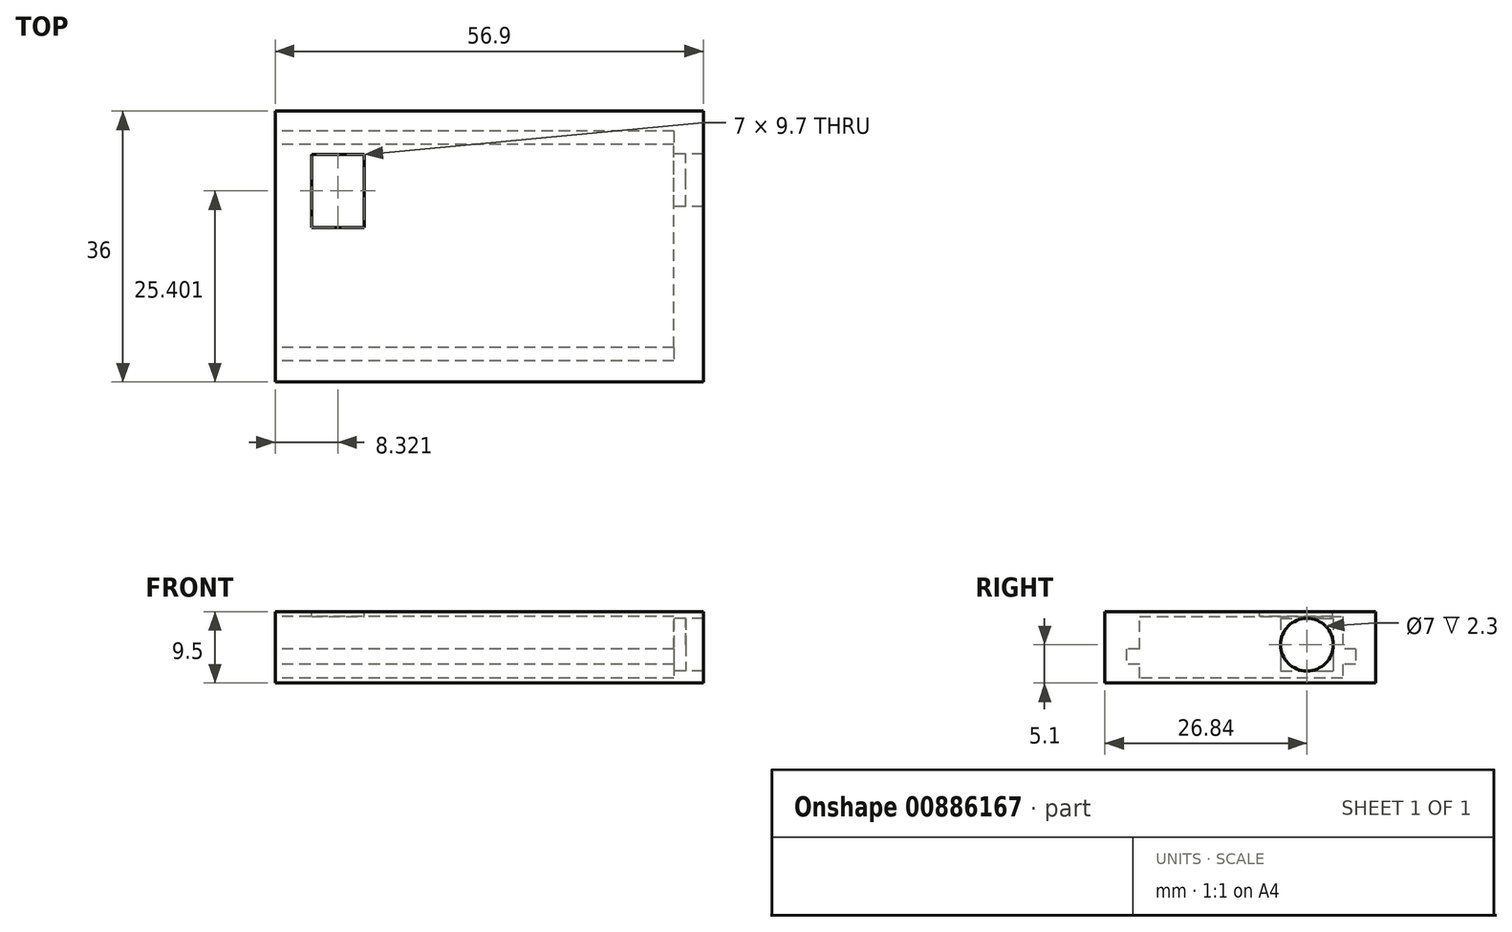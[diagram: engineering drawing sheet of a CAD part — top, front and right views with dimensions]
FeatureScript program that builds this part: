
annotation { "Feature Type Name" : "Feature", "Feature Type Description" : "" }
export const myFeature = defineFeature(function(context is Context, id is Id, definition is map)
    precondition{}
    {
        {
            var Q0;
            Q0=qCreatedBy(makeId("Top.planeOp"),FACE);
            var sketch = newSketch(context, id + "F0", { "sketchPlane" : qUnion([Q0])});
            skLineSegment(sketch, "E0.bottom", {"start": v(-26.94, 14.91) * mm, "end": v(23.06, 14.91) * mm});
            skLineSegment(sketch, "E0.top", {"start": v(-26.94, -15.09) * mm, "end": v(23.06, -15.09) * mm});
            skLineSegment(sketch, "E0.left", {"start": v(-26.94, 14.91) * mm, "end": v(-26.94, -15.09) * mm});
            skLineSegment(sketch, "E0.right", {"start": v(23.06, 14.91) * mm, "end": v(23.06, -15.09) * mm});
            skLineSegment(sketch, "E1.bottom", {"start": v(-34, -4.69) * mm, "end": v(-26.94, -4.69) * mm});
            skLineSegment(sketch, "E1.top", {"start": v(-34, -11.69) * mm, "end": v(-26.94, -11.69) * mm});
            skLineSegment(sketch, "E1.left", {"start": v(-34, -4.69) * mm, "end": v(-34, -11.69) * mm});
            skLineSegment(sketch, "E1.right", {"start": v(-26.94, -4.69) * mm, "end": v(-26.94, -11.69) * mm});
            skLineSegment(sketch, "E2.0", {"start": v(-26.94, 17.91) * mm, "end": v(26.06, 17.91) * mm});
            skLineSegment(sketch, "E2.2", {"start": v(-26.94, -18.09) * mm, "end": v(26.06, -18.09) * mm});
            skLineSegment(sketch, "E2.3", {"start": v(26.06, 17.91) * mm, "end": v(26.06, -18.09) * mm});
            skLineSegment(sketch, "E3", {"start": v(-26.94, 17.91) * mm, "end": v(-26.94, 14.91) * mm});
            skLineSegment(sketch, "E4", {"start": v(-26.94, -18.09) * mm, "end": v(-26.94, -15.09) * mm});
            skSolve(sketch);
        }
        {
            var Q0;
            {var subQ3=sQuery(id+"F0.wireOp",EDGE,"E0.bottom");Q0=makeQuery(id+"F0.imprint","IMPRINT",FACE,{"disambiguationData":[TD([[makeQuery(id+"F0.imprint","IMPRINT",EDGE,{"derivedFrom":subQ3}),-1.0]])]});}
            var Q1;
            {var subQ10=sQuery(id+"F0.wireOp",EDGE,"E0.bottom");Q1=makeQuery(id+"F0.imprint","IMPRINT",FACE,{"disambiguationData":[TD([[makeQuery(id+"F0.imprint","IMPRINT",EDGE,{"derivedFrom":subQ10}),1.0]])]});}
            extrude(context, id + "F1", {"entities" : qUnion([Q0, Q1]), "depth" : 6 * mm, "offsetDistance" : 25 * mm, "hasSecondDirection" : true, "secondDirectionOppositeDirection" : true, "secondDirectionDepth" : 3.5 * mm});
        }
        {
            var Q0;
            Q0=makeQuery(id+"F1.opExtrude","SWEPT_FACE",FACE,{"disambiguationData":[OSD([sQuery(id+"F0.wireOp",EDGE,"E0.left"),sQuery(id+"F0.wireOp",EDGE,"E1.right"),sQuery(id+"F0.wireOp",EDGE,"E3"),sQuery(id+"F0.wireOp",EDGE,"E4")])]});
            var sketch = newSketch(context, id + "F2", { "sketchPlane" : qUnion([Q0])});
            skLineSegment(sketch, "E5", {"start": v(-13.5, 5.34) * mm, "end": v(13.5, 5.34) * mm});
            skLineSegment(sketch, "E6", {"start": v(13.5, 5.34) * mm, "end": v(13.5, -2.86) * mm});
            skLineSegment(sketch, "E7", {"start": v(13.5, -2.86) * mm, "end": v(-13.5, -2.86) * mm});
            skLineSegment(sketch, "E8", {"start": v(-13.5, -2.86) * mm, "end": v(-13.5, 5.34) * mm});
            skPoint(sketch, "E9", {"position": v(0, -2.86) * mm});
            skLineSegment(sketch, "E10.bottom", {"start": v(15.25, -1) * mm, "end": v(-15.25, -1) * mm});
            skLineSegment(sketch, "E10.top", {"start": v(15.25, 1) * mm, "end": v(-15.25, 1) * mm});
            skLineSegment(sketch, "E10.left", {"start": v(15.25, -1) * mm, "end": v(15.25, 1) * mm});
            skLineSegment(sketch, "E10.right", {"start": v(-15.25, -1) * mm, "end": v(-15.25, 1) * mm});
            skPoint(sketch, "E10.middle", {"position": v(0, 0) * mm});
            skSolve(sketch);
        }
        {
            var Q0;
            {var subQ5=sQuery(id+"F2.wireOp",EDGE,"E10.left");Q0=makeQuery(id+"F2.imprint","IMPRINT",FACE,{"disambiguationData":[TD([[makeQuery(id+"F2.imprint","IMPRINT",EDGE,{"derivedFrom":subQ5}),1.0]])]});}
            var Q1;
            {var subQ0=sQuery(id+"F2.wireOp",EDGE,"E7");Q1=makeQuery(id+"F2.imprint","IMPRINT",FACE,{"disambiguationData":[TD([[makeQuery(id+"F2.imprint","IMPRINT",EDGE,{"derivedFrom":subQ0}),-1.0]])]});}
            var Q2;
            {var subQ5=sQuery(id+"F2.wireOp",EDGE,"E10.right");Q2=makeQuery(id+"F2.imprint","IMPRINT",FACE,{"disambiguationData":[TD([[makeQuery(id+"F2.imprint","IMPRINT",EDGE,{"derivedFrom":subQ5}),-1.0]])]});}
            var Q3;
            {var subQ0=sQuery(id+"F2.wireOp",EDGE,"E10.top");var subQ1=sQuery(id+"F2.wireOp",EDGE,"E6");var subQ2=makeQuery(id+"F2.imprint","INTERSECT",VERTEX,{"derivedFrom":[subQ1,subQ0]});Q3=makeQuery(id+"F2.imprint","IMPRINT",FACE,{"disambiguationData":[TD([[makeQuery(id+"F2.imprint","IMPRINT",EDGE,{"disambiguationData":[TD([[subQ2,-1.0]])],"derivedFrom":subQ1}),-1.0]])]});}
            var Q4;
            {var subQ0=sQuery(id+"F2.wireOp",EDGE,"E5");Q4=makeQuery(id+"F2.imprint","IMPRINT",FACE,{"disambiguationData":[TD([[makeQuery(id+"F2.imprint","IMPRINT",EDGE,{"derivedFrom":subQ0}),-1.0]])]});}
            extrude(context, id + "F3", {"entities" : qUnion([Q0, Q1, Q2, Q3, Q4]), "operationType" : NewBodyOperationType.REMOVE, "endBound" : BoundingType.THROUGH_ALL, "oppositeDirection" : true, "depth" : 25 * mm, "offsetDistance" : 25 * mm});
        }
        {
            var Q0;
            Q0=makeQuery(id+"F1.opExtrude","CAP_FACE",FACE,{"disambiguationData":[OSD([sQuery(id+"F0.wireOp",EDGE,"E2.0"),sQuery(id+"F0.wireOp",EDGE,"E2.1"),sQuery(id+"F0.wireOp",EDGE,"E2.2"),sQuery(id+"F0.wireOp",EDGE,"E2.3")])],"isStart":false});
            var sketch = newSketch(context, id + "F4", { "sketchPlane" : qUnion([Q0])});
            skLineSegment(sketch, "E11.bottom", {"start": v(-22.12, 12.16) * mm, "end": v(-15.12, 12.16) * mm});
            skLineSegment(sketch, "E11.top", {"start": v(-22.12, 2.46) * mm, "end": v(-15.12, 2.46) * mm});
            skLineSegment(sketch, "E11.left", {"start": v(-22.12, 12.16) * mm, "end": v(-22.12, 2.46) * mm});
            skLineSegment(sketch, "E11.right", {"start": v(-15.12, 12.16) * mm, "end": v(-15.12, 2.46) * mm});
            skSolve(sketch);
        }
        {
            var Q0;
            Q0=makeQuery(id+"F4.imprint","IMPRINT",FACE,{"disambiguationData":[TD([[makeQuery(id+"F4.imprint","IMPRINT",EDGE,{"derivedFrom":sQuery(id+"F4.wireOp",EDGE,"E11.bottom")}),-1.0]])]});
            extrude(context, id + "F5", {"entities" : qUnion([Q0]), "operationType" : NewBodyOperationType.REMOVE, "endBound" : BoundingType.UP_TO_NEXT, "oppositeDirection" : true, "depth" : 25 * mm, "offsetDistance" : 25 * mm});
        }
        {
            var Q0;
            Q0=makeQuery(id+"F1.opExtrude","SWEPT_FACE",FACE,{"disambiguationData":[OSD([sQuery(id+"F0.wireOp",EDGE,"E2.3")])]});
            var sketch = newSketch(context, id + "F6", { "sketchPlane" : qUnion([Q0])});
            skLineSegment(sketch, "E12.0", {"start": v(17.91, 6) * mm, "end": v(-18.09, 6) * mm});
            skLineSegment(sketch, "E12.1", {"start": v(17.91, 6) * mm, "end": v(17.91, -3.5) * mm});
            skLineSegment(sketch, "E12.2", {"start": v(17.91, -3.5) * mm, "end": v(-18.09, -3.5) * mm});
            skLineSegment(sketch, "E12.3", {"start": v(-18.09, 6) * mm, "end": v(-18.09, -3.5) * mm});
            skLineSegment(sketch, "E13", {"start": v(-18.09, 0) * mm, "end": v(17.91, 0) * mm, "construction": true});
            skPoint(sketch, "E13.endSnap0", {"position": v(-15.25, 0) * mm});
            skPoint(sketch, "E14", {"position": v(15.25, 0) * mm});
            skLineSegment(sketch, "E15.bottom", {"start": v(5.25, 5.1) * mm, "end": v(12.25, 5.1) * mm});
            skLineSegment(sketch, "E15.top", {"start": v(5.25, -1.9) * mm, "end": v(12.25, -1.9) * mm});
            skLineSegment(sketch, "E15.left", {"start": v(5.25, 5.1) * mm, "end": v(5.25, -1.9) * mm});
            skLineSegment(sketch, "E15.right", {"start": v(12.25, 5.1) * mm, "end": v(12.25, -1.9) * mm});
            skCircle(sketch, "E16", {"center": v(8.75, 1.6) * mm, "radius": 3.5 * mm});
            skSolve(sketch);
        }
        {
            var Q0;
            Q0=makeQuery(id+"F6.imprint","IMPRINT",FACE,{"disambiguationData":[TD([[makeQuery(id+"F6.imprint","IMPRINT",EDGE,{"derivedFrom":sQuery(id+"F6.wireOp",EDGE,"E12.0")}),1.0]])]});
            var Q1;
            {var subQ0=sQuery(id+"F6.wireOp",EDGE,"E15.left");var subQ1=sQuery(id+"F6.wireOp",EDGE,"E15.bottom");var subQ2=makeQuery(id+"F6.imprint","INTERSECT",VERTEX,{"derivedFrom":[subQ1,subQ0]});Q1=makeQuery(id+"F6.imprint","IMPRINT",FACE,{"disambiguationData":[TD([[makeQuery(id+"F6.imprint","IMPRINT",EDGE,{"disambiguationData":[TD([[subQ2,-1.0]])],"derivedFrom":subQ1}),-1.0]])]});}
            var Q2;
            {var subQ0=sQuery(id+"F6.wireOp",EDGE,"E15.right");var subQ1=sQuery(id+"F6.wireOp",EDGE,"E15.bottom");var subQ2=makeQuery(id+"F6.imprint","INTERSECT",VERTEX,{"derivedFrom":[subQ1,subQ0]});Q2=makeQuery(id+"F6.imprint","IMPRINT",FACE,{"disambiguationData":[TD([[makeQuery(id+"F6.imprint","IMPRINT",EDGE,{"disambiguationData":[TD([[subQ2,1.0]])],"derivedFrom":subQ1}),-1.0]])]});}
            var Q3;
            {var subQ0=sQuery(id+"F6.wireOp",EDGE,"E15.right");var subQ1=sQuery(id+"F6.wireOp",EDGE,"E15.top");var subQ2=makeQuery(id+"F6.imprint","INTERSECT",VERTEX,{"derivedFrom":[subQ1,subQ0]});Q3=makeQuery(id+"F6.imprint","IMPRINT",FACE,{"disambiguationData":[TD([[makeQuery(id+"F6.imprint","IMPRINT",EDGE,{"disambiguationData":[TD([[subQ2,1.0]])],"derivedFrom":subQ1}),1.0]])]});}
            var Q4;
            {var subQ0=sQuery(id+"F6.wireOp",EDGE,"E15.left");var subQ1=sQuery(id+"F6.wireOp",EDGE,"E15.top");var subQ2=makeQuery(id+"F6.imprint","INTERSECT",VERTEX,{"derivedFrom":[subQ1,subQ0]});Q4=makeQuery(id+"F6.imprint","IMPRINT",FACE,{"disambiguationData":[TD([[makeQuery(id+"F6.imprint","IMPRINT",EDGE,{"disambiguationData":[TD([[subQ2,-1.0]])],"derivedFrom":subQ1}),1.0]])]});}
            var Q5;
            {var subQ13=makeQuery(id+"F1.opExtrude","SWEPT_FACE",FACE,{"disambiguationData":[OSD([sQuery(id+"F0.wireOp",EDGE,"E2.3")])]});var subQ14=sQuery(id+"F2.wireOp",EDGE,"E5");Q5=makeQuery(id+"F6.imprint","IMPRINT",FACE,{"disambiguationData":[TD([[makeQuery(id+"F6.imprint","IMPRINT",EDGE,{"derivedFrom":makeQuery(id+"F3.boolean.opBoolean","INTERSECT",EDGE,{"derivedFrom":[subQ13,makeQuery(id+"F3.opExtrude","SWEPT_FACE",FACE,{"disambiguationData":[OSD([subQ14])]})]})}),-1.0]])]});}
            extrude(context, id + "F7", {"entities" : qUnion([Q0, Q1, Q2, Q3, Q4, Q5]), "operationType" : NewBodyOperationType.ADD, "depth" : 3.9 * mm, "offsetDistance" : 25 * mm});
        }
        {
            var Q0;
            {var subQ0=sQuery(id+"F6.wireOp",EDGE,"E15.left");var subQ1=sQuery(id+"F6.wireOp",EDGE,"E15.bottom");var subQ2=makeQuery(id+"F6.imprint","INTERSECT",VERTEX,{"derivedFrom":[subQ1,subQ0]});Q0=makeQuery(id+"F6.imprint","IMPRINT",FACE,{"disambiguationData":[TD([[makeQuery(id+"F6.imprint","IMPRINT",EDGE,{"disambiguationData":[TD([[subQ2,-1.0]])],"derivedFrom":subQ1}),-1.0]])]});}
            var Q1;
            {var subQ0=sQuery(id+"F6.wireOp",EDGE,"E15.right");var subQ1=sQuery(id+"F6.wireOp",EDGE,"E15.bottom");var subQ2=makeQuery(id+"F6.imprint","INTERSECT",VERTEX,{"derivedFrom":[subQ1,subQ0]});Q1=makeQuery(id+"F6.imprint","IMPRINT",FACE,{"disambiguationData":[TD([[makeQuery(id+"F6.imprint","IMPRINT",EDGE,{"disambiguationData":[TD([[subQ2,1.0]])],"derivedFrom":subQ1}),-1.0]])]});}
            var Q2;
            {var subQ0=sQuery(id+"F6.wireOp",EDGE,"E15.right");var subQ1=sQuery(id+"F6.wireOp",EDGE,"E15.top");var subQ2=makeQuery(id+"F6.imprint","INTERSECT",VERTEX,{"derivedFrom":[subQ1,subQ0]});Q2=makeQuery(id+"F6.imprint","IMPRINT",FACE,{"disambiguationData":[TD([[makeQuery(id+"F6.imprint","IMPRINT",EDGE,{"disambiguationData":[TD([[subQ2,1.0]])],"derivedFrom":subQ1}),1.0]])]});}
            var Q3;
            {var subQ0=sQuery(id+"F6.wireOp",EDGE,"E15.left");var subQ1=sQuery(id+"F6.wireOp",EDGE,"E15.top");var subQ2=makeQuery(id+"F6.imprint","INTERSECT",VERTEX,{"derivedFrom":[subQ1,subQ0]});Q3=makeQuery(id+"F6.imprint","IMPRINT",FACE,{"disambiguationData":[TD([[makeQuery(id+"F6.imprint","IMPRINT",EDGE,{"disambiguationData":[TD([[subQ2,-1.0]])],"derivedFrom":subQ1}),1.0]])]});}
            extrude(context, id + "F8", {"entities" : qUnion([Q0, Q1, Q2, Q3]), "operationType" : NewBodyOperationType.REMOVE, "depth" : 1.6 * mm, "offsetDistance" : 25 * mm});
        }
    });
